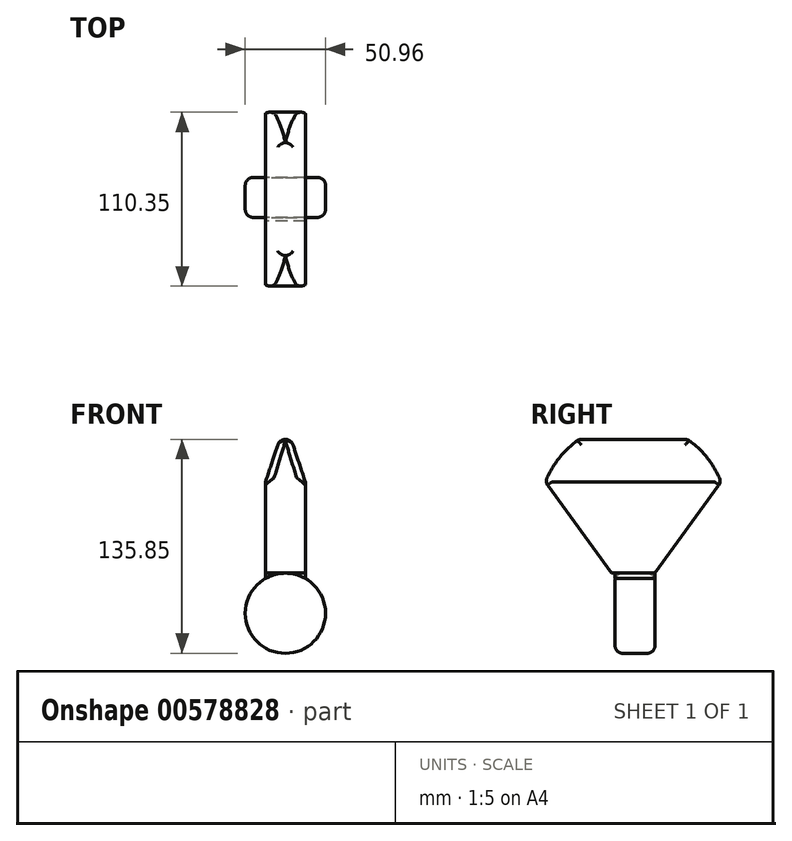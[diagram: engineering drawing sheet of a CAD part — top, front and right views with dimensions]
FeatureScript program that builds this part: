
annotation { "Feature Type Name" : "Feature", "Feature Type Description" : "" }
export const myFeature = defineFeature(function(context is Context, id is Id, definition is map)
    precondition{}
    {
        {
            var Q0;
            Q0=qCreatedBy(makeId("Front.planeOp"),FACE);
            var sketch = newSketch(context, id + "F0", { "sketchPlane" : qUnion([Q0])});
            skCircle(sketch, "E0", {"center": v(0, 0) * mm, "radius": 25.48 * mm});
            skSolve(sketch);
        }
        {
            var Q0;
            Q0 = qSketchRegion(id + "F0", true);
            extrude(context, id + "F1", {"entities" : qUnion([Q0]), "endBound" : BoundingType.SYMMETRIC, "depth" : 25.4 * mm, "offsetDistance" : 25.4 * mm});
        }
        {
            var Q0;
            Q0=qCreatedBy(makeId("Right.planeOp"),FACE);
            var sketch = newSketch(context, id + "F2", { "sketchPlane" : qUnion([Q0])});
            skLineSegment(sketch, "E1", {"start": v(-14.87, 25.48) * mm, "end": v(12.7, 25.48) * mm});
            skLineSegment(sketch, "E2", {"start": v(-14.87, 25.48) * mm, "end": v(-56.99, 83.34) * mm});
            skLineSegment(sketch, "E3", {"start": v(12.7, 25.48) * mm, "end": v(54.81, 83.34) * mm});
            skArc(sketch, "E4", {"start": v(54.81, 83.34) * mm, "mid": v(-1.09, 121.3) * mm, "end": v(-56.99, 83.34) * mm});
            skSolve(sketch);
        }
        {
            var Q0;
            Q0 = qSketchRegion(id + "F2", true);
            extrude(context, id + "F3", {"entities" : qUnion([Q0]), "operationType" : NewBodyOperationType.ADD, "endBound" : BoundingType.SYMMETRIC, "depth" : 25.4 * mm, "offsetDistance" : 25.4 * mm});
        }
        {
            var Q0;
            Q0=qCreatedBy(makeId("Front.planeOp"),FACE);
            var sketch = newSketch(context, id + "F4", { "sketchPlane" : qUnion([Q0])});
            skLineSegment(sketch, "E5.0", {"start": v(12.7, 25.48) * mm, "end": v(-12.7, 25.48) * mm});
            skArc(sketch, "E6.0", {"start": v(12.85, 22) * mm, "mid": v(0.08, 25.48) * mm, "end": v(-12.7, 22.09) * mm});
            skLineSegment(sketch, "E7", {"start": v(12.85, 22) * mm, "end": v(12.7, 25.48) * mm});
            skLineSegment(sketch, "E8", {"start": v(-12.7, 25.48) * mm, "end": v(-12.7, 22.09) * mm});
            skArc(sketch, "E9", {"start": v(12.85, 22) * mm, "mid": v(0.08, 25.43) * mm, "end": v(-12.7, 22.09) * mm});
            skSolve(sketch);
        }
        {
            var Q0;
            Q0 = qSketchRegion(id + "F4", true);
            extrude(context, id + "F5", {"entities" : qUnion([Q0]), "endBound" : BoundingType.SYMMETRIC, "depth" : 25.4 * mm, "offsetDistance" : 25.4 * mm});
        }
        {
            var Q0;
            Q0=qCreatedBy(makeId("Front.planeOp"),FACE);
            var sketch = newSketch(context, id + "F6", { "sketchPlane" : qUnion([Q0])});
            skLineSegment(sketch, "E10.0", {"start": v(-12.7, 83.34) * mm, "end": v(-12.7, 121.3) * mm});
            skLineSegment(sketch, "E11", {"start": v(-12.7, 121.3) * mm, "end": v(12.7, 121.3) * mm});
            skLineSegment(sketch, "E12", {"start": v(-12.7, 83.34) * mm, "end": v(0, 121.3) * mm});
            skLineSegment(sketch, "E13", {"start": v(0, 121.3) * mm, "end": v(-12.7, 121.3) * mm});
            skSolve(sketch);
        }
        {
            var Q0;
            Q0 = qSketchRegion(id + "F6", true);
            extrude(context, id + "F7", {"entities" : qUnion([Q0]), "operationType" : NewBodyOperationType.REMOVE, "endBound" : BoundingType.SYMMETRIC, "depth" : 254 * mm, "offsetDistance" : 25.4 * mm});
        }
        {
            var Q0;
            Q0=qCreatedBy(makeId("Front.planeOp"),FACE);
            var sketch = newSketch(context, id + "F8", { "sketchPlane" : qUnion([Q0])});
            skLineSegment(sketch, "E14", {"start": v(0, 121.3) * mm, "end": v(12.7, 121.3) * mm});
            skLineSegment(sketch, "E15.0", {"start": v(12.7, 83.34) * mm, "end": v(12.7, 121.3) * mm});
            skLineSegment(sketch, "E16", {"start": v(12.7, 83.34) * mm, "end": v(0, 121.3) * mm});
            skLineSegment(sketch, "E17", {"start": v(12.7, 121.3) * mm, "end": v(12.7, 83.34) * mm});
            skSolve(sketch);
        }
        {
            var Q0;
            Q0 = qSketchRegion(id + "F8", true);
            extrude(context, id + "F9", {"entities" : qUnion([Q0]), "operationType" : NewBodyOperationType.REMOVE, "endBound" : BoundingType.SYMMETRIC, "depth" : 254 * mm, "offsetDistance" : 25.4 * mm});
        }
        {
            var Q0;
            {var subQ0=sQuery(id+"F2.wireOp",EDGE,"E4");var subQ1=makeQuery(id+"F3.opExtrude","SWEPT_FACE",FACE,{"disambiguationData":[OSD([subQ0])]});var subQ2=sQuery(id+"F2.wireOp",EDGE,"E3");Q0=makeQuery(id+"F9.boolean.opBoolean","SPLIT",FACE,{"disambiguationData":[TD([makeQuery(id+"F3.opExtrude","SWEPT_FACE",FACE,{"disambiguationData":[OSD([subQ2])]})])],"derivedFrom":subQ1});}
            var Q1;
            {var subQ0=sQuery(id+"F2.wireOp",EDGE,"E4");var subQ1=makeQuery(id+"F3.opExtrude","SWEPT_FACE",FACE,{"disambiguationData":[OSD([subQ0])]});var subQ2=sQuery(id+"F2.wireOp",EDGE,"E2");Q1=makeQuery(id+"F9.boolean.opBoolean","SPLIT",FACE,{"disambiguationData":[TD([makeQuery(id+"F3.opExtrude","SWEPT_FACE",FACE,{"disambiguationData":[OSD([subQ2])]})])],"derivedFrom":subQ1});}
            fillet(context, id + "F10", {"entities" : qUnion([Q0, Q1]), "radius" : 5.08 * mm, "tangentPropagation" : true, "allowEdgeOverflow" : false});
        }
        {
            var Q0;
            Q0=makeQuery(id+"F1.opExtrude","CAP_EDGE",EDGE,{"disambiguationData":[OSD([sQuery(id+"F0.wireOp",EDGE,"E0")])],"isStart":true});
            var Q1;
            Q1=makeQuery(id+"F1.opExtrude","CAP_FACE",FACE,{"disambiguationData":[OSD([sQuery(id+"F0.wireOp",EDGE,"E0")])],"isStart":false});
            fillet(context, id + "F11", {"entities" : qUnion([Q0, Q1]), "radius" : 5.08 * mm, "tangentPropagation" : true, "allowEdgeOverflow" : false});
        }
    });
